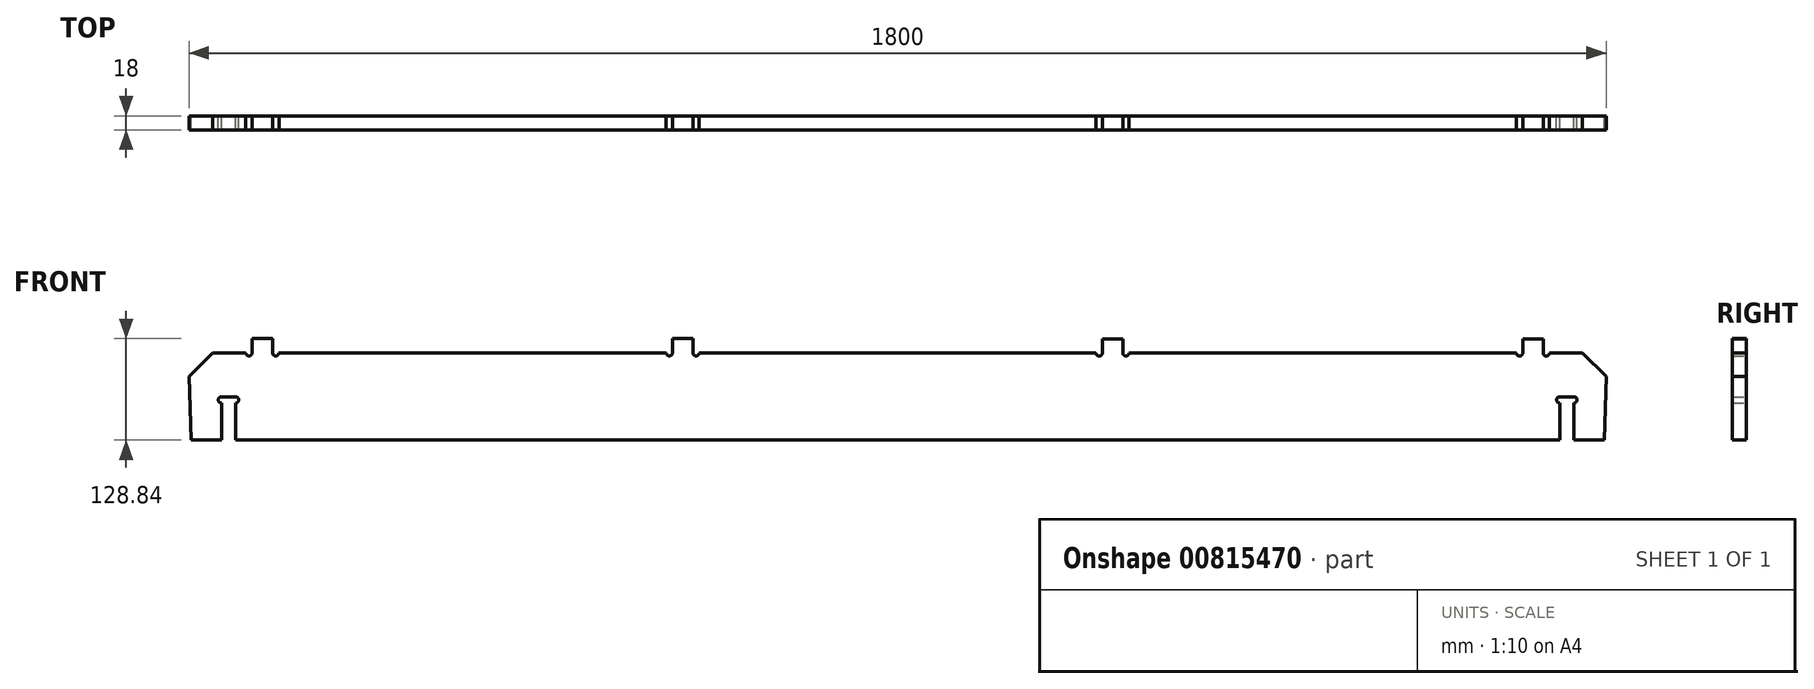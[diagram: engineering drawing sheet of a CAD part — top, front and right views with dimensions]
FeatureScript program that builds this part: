
annotation { "Feature Type Name" : "Feature", "Feature Type Description" : "" }
export const myFeature = defineFeature(function(context is Context, id is Id, definition is map)
    precondition{}
    {
        {
            var Q0;
            Q0=qCreatedBy(makeId("Front.planeOp"),FACE);
            var sketch = newSketch(context, id + "F0", { "sketchPlane" : qUnion([Q0])});
            skPoint(sketch, "E0.middle", {"position": v(0, 0) * mm});
            skLineSegment(sketch, "E1.right", {"start": v(1445, 379) * mm, "end": v(1445, 361) * mm});
            skPoint(sketch, "E2.start.orphan", {"position": v(-195, 368.73) * mm});
            skPoint(sketch, "E3.start.orphan", {"position": v(1445, 370) * mm});
            skLineSegment(sketch, "E4", {"start": v(-203, 361.18) * mm, "end": v(-244.9, 361.18) * mm});
            skPoint(sketch, "E5.orphan", {"position": v(-274.99, 376.28) * mm});
            skLineSegment(sketch, "E6", {"start": v(1453, 361) * mm, "end": v(1494.9, 361) * mm});
            skPoint(sketch, "E7.orphan", {"position": v(274.99, 376.28) * mm});
            skArc(sketch, "E8", {"start": v(1445, 361) * mm, "mid": v(1449, 357) * mm, "end": v(1453, 361) * mm});
            skArc(sketch, "E9", {"start": v(-203, 361.18) * mm, "mid": v(-199, 357.18) * mm, "end": v(-195, 361.18) * mm});
            skLineSegment(sketch, "E10.top", {"start": v(-244.9, 361.18) * mm, "end": v(-203, 361.18) * mm});
            skLineSegment(sketch, "E11", {"start": v(-244.9, 361.18) * mm, "end": v(-274.99, 331.07) * mm});
            skLineSegment(sketch, "E12", {"start": v(-274.99, 331.07) * mm, "end": v(-272.7, 250.34) * mm});
            skPoint(sketch, "E13.start.orphan", {"position": v(-274.99, -376.28) * mm});
            skLineSegment(sketch, "E14", {"start": v(1525.01, 331) * mm, "end": v(1522.73, 250.34) * mm});
            skPoint(sketch, "E15.start.orphan", {"position": v(274.99, -376.28) * mm});
            skPoint(sketch, "E16.left.end.orphan", {"position": v(-195, 361.18) * mm});
            skPoint(sketch, "E17.orphan", {"position": v(-195, 376.28) * mm});
            skLineSegment(sketch, "E18", {"start": v(-195, 361.18) * mm, "end": v(-195, 379.18) * mm});
            skLineSegment(sketch, "E19", {"start": v(-195, 379.18) * mm, "end": v(-169, 379.18) * mm});
            skLineSegment(sketch, "E20", {"start": v(-169, 379.18) * mm, "end": v(-169, 361.18) * mm});
            skLineSegment(sketch, "E21.top", {"start": v(-233.99, 361.18) * mm, "end": v(-215.99, 361.18) * mm});
            skLineSegment(sketch, "E22", {"start": v(1505.01, -376.36) * mm, "end": v(1484.02, -375.76) * mm});
            skLineSegment(sketch, "E23.top", {"start": v(1484.02, -7.69) * mm, "end": v(1466.02, -7.69) * mm});
            skLineSegment(sketch, "E23.left", {"start": v(1484.02, -375.76) * mm, "end": v(1484.02, -15.69) * mm});
            skLineSegment(sketch, "E23.right", {"start": v(1466.02, -375.69) * mm, "end": v(1466.02, -15.69) * mm});
            skLineSegment(sketch, "E24.top", {"start": v(1494.9, 361) * mm, "end": v(1466.02, 361) * mm});
            skLineSegment(sketch, "E25", {"start": v(1445, 379) * mm, "end": v(1419, 379) * mm});
            skLineSegment(sketch, "E26", {"start": v(1419, 379) * mm, "end": v(1419, 361) * mm});
            skArc(sketch, "E27", {"start": v(-169, 361.18) * mm, "mid": v(-165, 357.18) * mm, "end": v(-161, 361.18) * mm});
            skLineSegment(sketch, "E28", {"start": v(1445.01, -376.28) * mm, "end": v(1466.02, -375.69) * mm});
            skArc(sketch, "E29", {"start": v(1411, 361) * mm, "mid": v(1415, 357) * mm, "end": v(1419, 361) * mm});
            skLineSegment(sketch, "E30", {"start": v(-274.99, 331.07) * mm, "end": v(-274.99, 376.28) * mm});
            skLineSegment(sketch, "E31", {"start": v(-134.99, 250.34) * mm, "end": v(1385.01, 250.34) * mm});
            skLineSegment(sketch, "E32", {"start": v(-161, 361.18) * mm, "end": v(331, 361.18) * mm});
            skLineSegment(sketch, "E33", {"start": v(1411, 361) * mm, "end": v(919, 361) * mm});
            skLineSegment(sketch, "E34.top", {"start": v(911, 379) * mm, "end": v(885, 379) * mm});
            skLineSegment(sketch, "E34.left", {"start": v(911, 361) * mm, "end": v(911, 379) * mm});
            skLineSegment(sketch, "E34.right", {"start": v(885, 361) * mm, "end": v(885, 379) * mm});
            skLineSegment(sketch, "E35.top", {"start": v(339, 379.18) * mm, "end": v(365, 379.18) * mm});
            skLineSegment(sketch, "E35.left", {"start": v(339, 361.18) * mm, "end": v(339, 379.18) * mm});
            skLineSegment(sketch, "E35.right", {"start": v(365, 361.18) * mm, "end": v(365, 379.18) * mm});
            skArc(sketch, "E36", {"start": v(331, 361.18) * mm, "mid": v(335, 357.18) * mm, "end": v(339, 361.18) * mm});
            skArc(sketch, "E37", {"start": v(365, 361.18) * mm, "mid": v(369, 357.17) * mm, "end": v(373, 361.17) * mm});
            skLineSegment(sketch, "E38.trimOffspring", {"start": v(373, 361.17) * mm, "end": v(877, 361) * mm});
            skArc(sketch, "E39", {"start": v(911, 361) * mm, "mid": v(915, 357) * mm, "end": v(919, 361) * mm});
            skArc(sketch, "E40", {"start": v(877, 361) * mm, "mid": v(881, 357) * mm, "end": v(885, 361) * mm});
            skArc(sketch, "E41", {"start": v(1484.02, -15.69) * mm, "mid": v(1488.02, -11.69) * mm, "end": v(1484.02, -7.69) * mm});
            skArc(sketch, "E42", {"start": v(1466.02, -7.69) * mm, "mid": v(1462.02, -11.69) * mm, "end": v(1466.02, -15.69) * mm});
            skLineSegment(sketch, "E43", {"start": v(1525.01, 331) * mm, "end": v(1525.01, 421.85) * mm});
            skLineSegment(sketch, "E44", {"start": v(-134.99, 250.34) * mm, "end": v(-215.99, 250.34) * mm});
            skLineSegment(sketch, "E45", {"start": v(-233.99, 250.34) * mm, "end": v(-233.99, 297.34) * mm});
            skLineSegment(sketch, "E46", {"start": v(-233.99, 305.34) * mm, "end": v(-215.99, 305.34) * mm});
            skLineSegment(sketch, "E47", {"start": v(-215.99, 297.34) * mm, "end": v(-215.99, 250.34) * mm});
            skArc(sketch, "E48", {"start": v(-233.99, 305.34) * mm, "mid": v(-237.99, 301.34) * mm, "end": v(-233.99, 297.34) * mm});
            skArc(sketch, "E49", {"start": v(-215.99, 297.34) * mm, "mid": v(-211.99, 301.34) * mm, "end": v(-215.99, 305.34) * mm});
            skLineSegment(sketch, "E50.trimOffspring", {"start": v(-233.99, 250.34) * mm, "end": v(-272.7, 250.34) * mm});
            skPoint(sketch, "E51.top.end.orphan", {"position": v(-215.99, -8.28) * mm});
            skLineSegment(sketch, "E52", {"start": v(1385.01, 250.34) * mm, "end": v(1466.02, 250.34) * mm});
            skLineSegment(sketch, "E53", {"start": v(1466.02, 250.34) * mm, "end": v(1466.02, 297.34) * mm});
            skLineSegment(sketch, "E54", {"start": v(1466.02, 305.34) * mm, "end": v(1484.02, 305.34) * mm});
            skLineSegment(sketch, "E55", {"start": v(1484.02, 297.34) * mm, "end": v(1484.02, 250.34) * mm});
            skLineSegment(sketch, "E56", {"start": v(1494.9, 361) * mm, "end": v(1525.01, 331) * mm});
            skArc(sketch, "E57", {"start": v(1466.02, 305.34) * mm, "mid": v(1462.02, 301.34) * mm, "end": v(1466.02, 297.34) * mm});
            skArc(sketch, "E58", {"start": v(1484.02, 297.34) * mm, "mid": v(1488.02, 301.34) * mm, "end": v(1484.02, 305.34) * mm});
            skLineSegment(sketch, "E59.trimOffspring", {"start": v(1484.02, 250.34) * mm, "end": v(1522.73, 250.34) * mm});
            skSolve(sketch);
        }
        {
            var Q0;
            Q0=makeQuery(id+"F0.imprint","IMPRINT",FACE,{"disambiguationData":[TD([[makeQuery(id+"F0.imprint","IMPRINT",EDGE,{"derivedFrom":sQuery(id+"F0.wireOp",EDGE,"E1.right")}),-1.0]])]});
            extrude(context, id + "F1", {"entities" : qUnion([Q0]), "depth" : 18 * mm, "offsetDistance" : 25 * mm});
        }
    });
